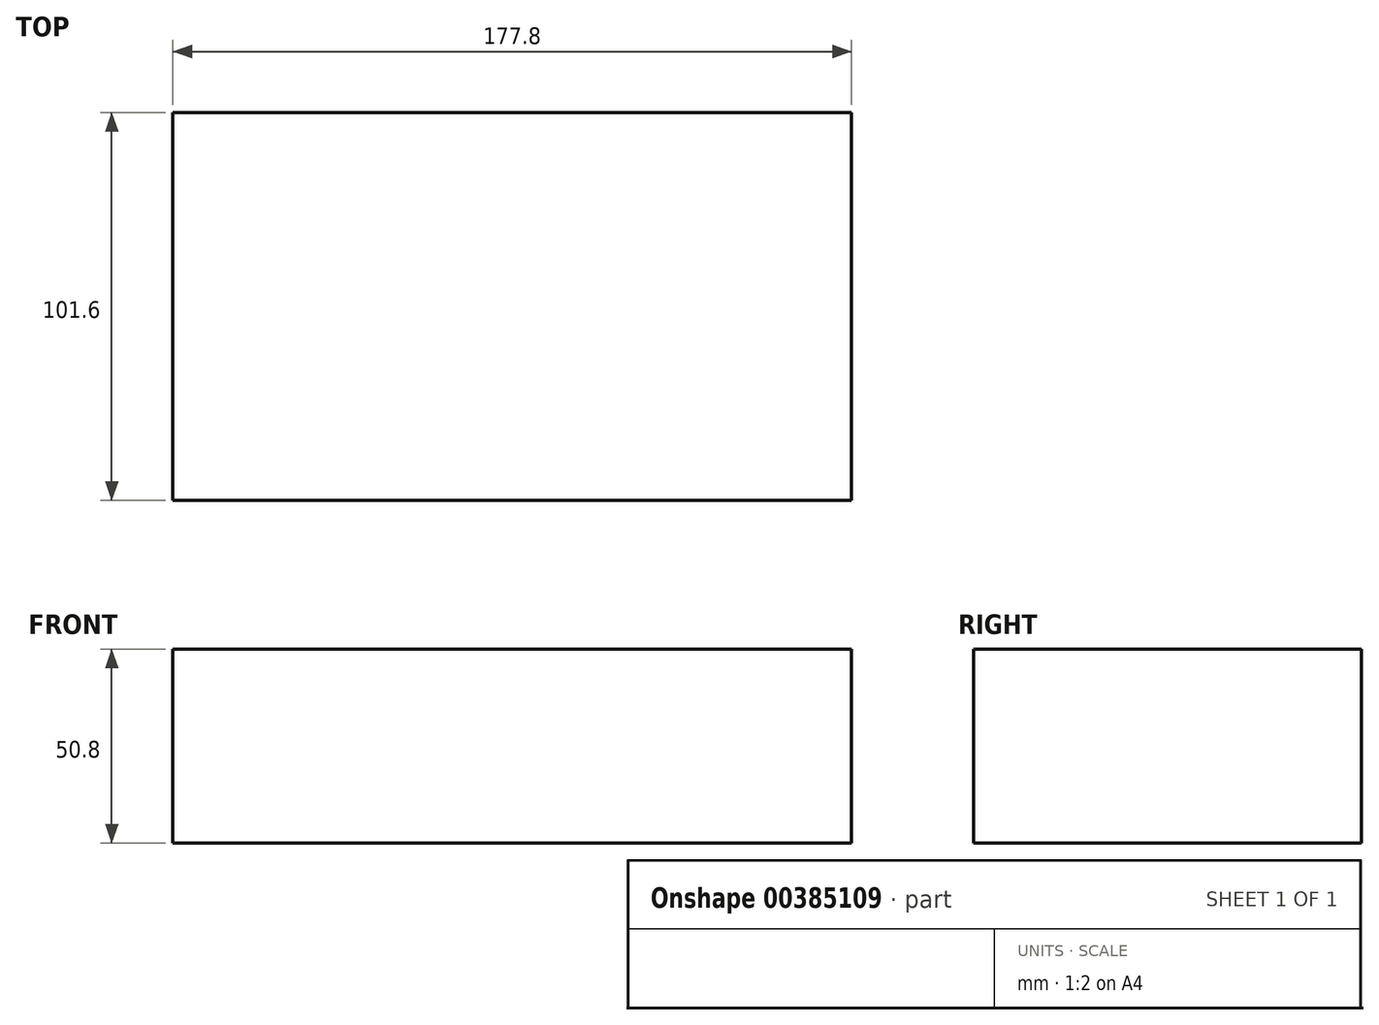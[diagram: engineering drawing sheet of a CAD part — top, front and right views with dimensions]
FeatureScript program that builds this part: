
annotation { "Feature Type Name" : "Feature", "Feature Type Description" : "" }
export const myFeature = defineFeature(function(context is Context, id is Id, definition is map)
    precondition{}
    {
        {
            var Q0;
            Q0=qCreatedBy(makeId("Front.planeOp"),FACE);
            var sketch = newSketch(context, id + "F0", { "sketchPlane" : qUnion([Q0])});
            skLineSegment(sketch, "E0.bottom", {"start": v(88.9, 25.4) * mm, "end": v(-88.9, 25.4) * mm});
            skLineSegment(sketch, "E0.top", {"start": v(88.9, -25.4) * mm, "end": v(-88.9, -25.4) * mm});
            skLineSegment(sketch, "E0.left", {"start": v(88.9, 25.4) * mm, "end": v(88.9, -25.4) * mm});
            skLineSegment(sketch, "E0.right", {"start": v(-88.9, 25.4) * mm, "end": v(-88.9, -25.4) * mm});
            skPoint(sketch, "E0.middle", {"position": v(0, 0) * mm});
            skSolve(sketch);
        }
        {
            var Q0;
            Q0 = qSketchRegion(id + "F0", true);
            extrude(context, id + "F1", {"entities" : qUnion([Q0]), "depth" : 101.6 * mm});
        }
    });
